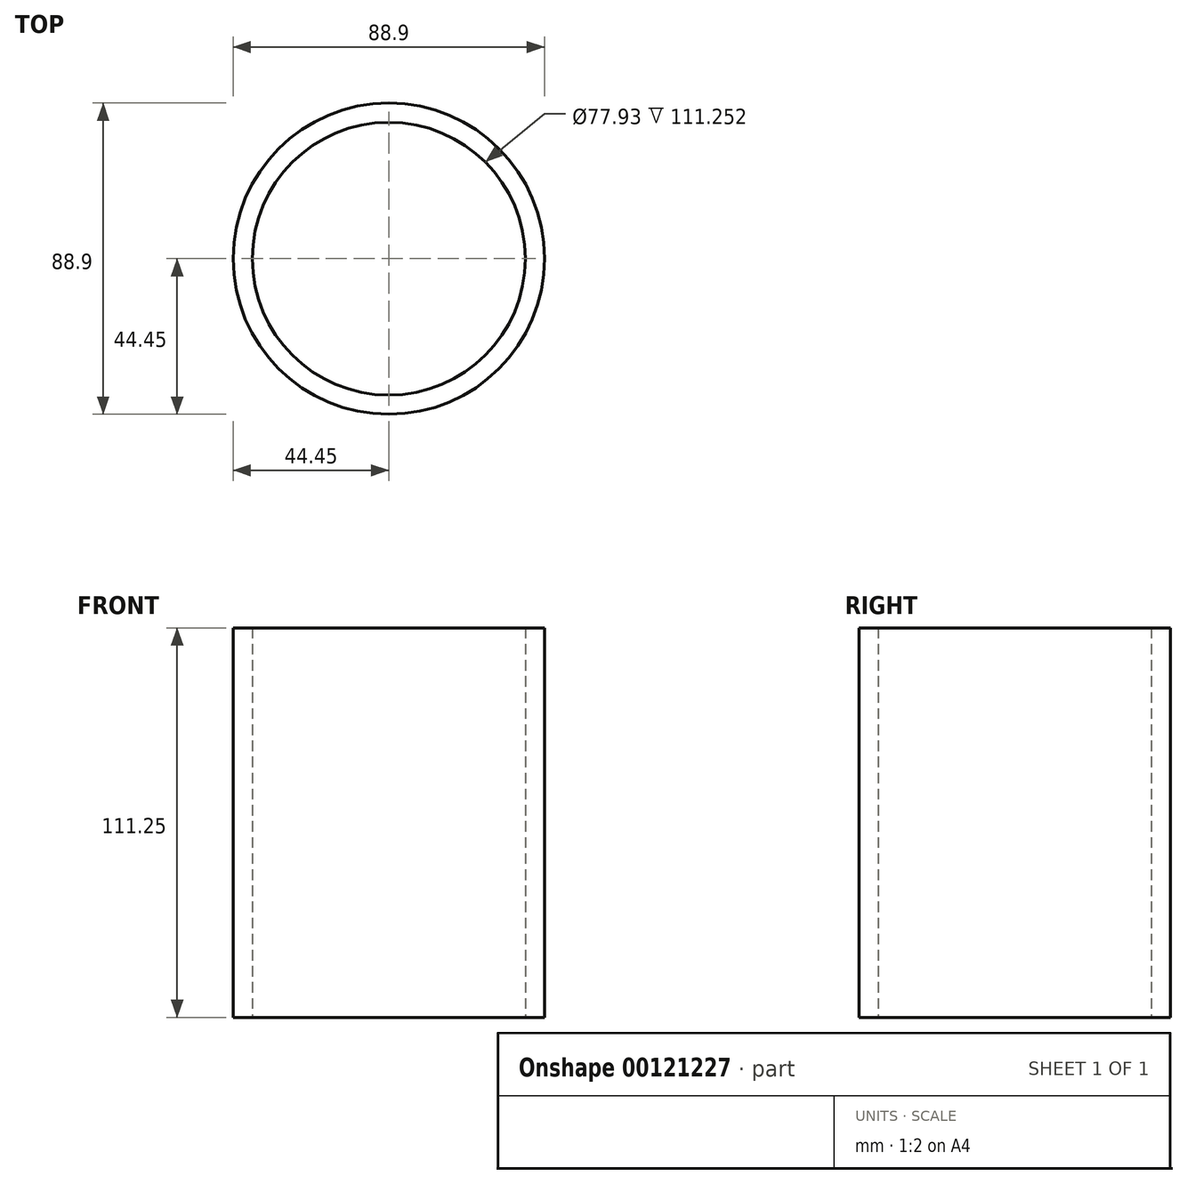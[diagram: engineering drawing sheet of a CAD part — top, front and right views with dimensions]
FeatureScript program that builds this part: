
annotation { "Feature Type Name" : "Feature", "Feature Type Description" : "" }
export const myFeature = defineFeature(function(context is Context, id is Id, definition is map)
    precondition{}
    {
        {
            var Q0;
            Q0=qCreatedBy(makeId("Top.planeOp"),FACE);
            var sketch = newSketch(context, id + "F0", { "sketchPlane" : qUnion([Q0])});
            skCircle(sketch, "E0", {"center": v(0, 0) * mm, "radius": 44.45 * mm});
            skCircle(sketch, "E1", {"center": v(0, 0) * mm, "radius": 38.96 * mm});
            skSolve(sketch);
        }
        {
            var Q0;
            Q0=qSketchRegion(id+"F0",true);
            extrude(context, id + "F1", {"entities" : qUnion([Q0]), "depth" : 111.25 * mm});
        }
    });
